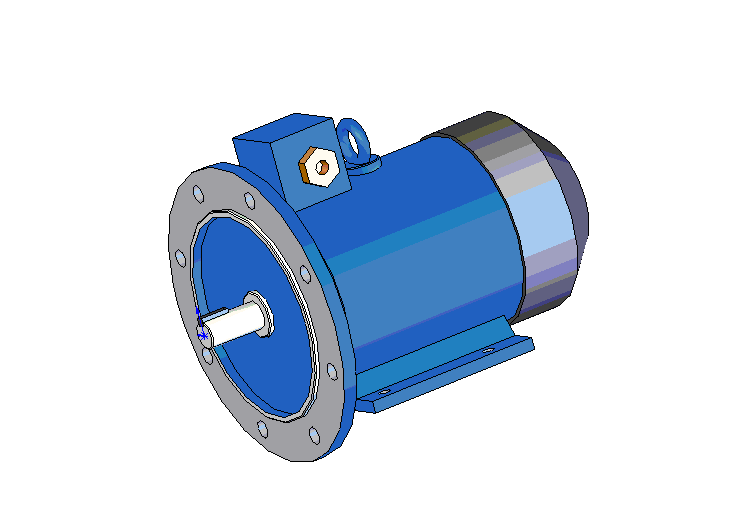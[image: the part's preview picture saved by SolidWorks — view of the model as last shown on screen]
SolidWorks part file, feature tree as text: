
SOLIDWORKS PART (.sldprt)
format: sldprt  version: not decoded by parser v0  size: 766,464 bytes
history: native  units: mm
features: sketch x18, extrude x12, plane x4, cut_extrude x4, chamfer x3, material x1, sweep x1 (+10 scaffold rows collapsed)
feature tree (53):
  scaffold x10  (default folders/planes/origin — collapsed)
  material  "Ст.3 ГОСТ 380-88"
  plane  "Спереди"
  plane  "Сверху"
  plane  "Справа"
  sketch  "Эскиз1"  dims[D1=24.0mm]
  extrude  "Вытянуть1"  Depth=50mm
  sketch  "Эскиз2"  dims[D1=7.0mm D2=7.0mm D3=27.0mm]
  extrude  "Вытянуть2"  Depth=25mm
  sketch  "Эскиз3"  dims[D1=250.0mm]
  extrude  "Вытянуть3"  Depth=12mm
  sketch  "Эскиз4"  dims[D1=180.0mm D2=170.0mm]
  extrude  "Вытянуть4"  Depth=4mm
  sketch  "Эскиз5"  dims[D1=170.0mm D2=40.0mm]
  cut_extrude  "Вырез-Вытянуть1"  Depth=4mm
  chamfer  "Фаска1"  Distance=1mm Angle=45deg
  sketch  "Эскиз6"  dims[c1.D2=15.0mm c1.D1=~150.356167mm c2.D1=22.5deg c2.D3=107.5mm c2.D4=107.5mm c2.D5=107.5mm]
  cut_extrude  "Вырез-Вытянуть2"  [1 undecoded]
  sketch  "Эскиз7"  dims[D1=150.0mm]
  extrude  "Вытянуть5"  Depth=24mm
  sketch  "Эскиз8"  dims[D1=160.0mm]
  extrude  "Вытянуть6"  Depth=167mm
  sketch  "Эскиз9"  dims[D1=166.0mm]
  extrude  "Вытянуть7"  Depth=84mm
  chamfer  "Фаска2"  Distance=34mm Angle=45deg
  sketch  "Эскиз10"  dims[c1.D1=10.0mm c1.D2=84.0mm c1.D3=10.0mm c1.D4=~41.116657mm c2.D4=30.0deg c2.D5=90.0mm c2.D6=58.0mm]
  extrude  "Вытянуть8"  Depth=153mm
  sketch  "Эскиз11"  dims[D2=10.0mm D1=106.0mm D3=70.0mm D4=90.0deg D5=100.0mm D6=206.0mm D7=140.0mm]
  cut_extrude  "Вырез-Вытянуть3"  [1 undecoded]
  sketch  "Эскиз12"  dims[D1=60.0mm D2=60.0mm D3=1.0mm]
  extrude  "Вытянуть9"  Depth=134.5mm
  sketch  "Эскиз13"  dims[D1=35.0mm D2=175.0mm]
  extrude  "Вытянуть10"  Depth=85.5mm
  chamfer  "Фаска3"  Distance=1mm Angle=45deg
  plane  "Плоскость1"  Offset=175mm
  sketch  "Эскиз14"  dims[D1=32.0mm]
  sketch  "Эскиз15"  dims[D1=10.0mm D2=32.0mm]
  sweep  "По траектории1"
  sketch  "Эскиз16"  dims[c1.D1=~12.488278mm c1.D3=18.0mm c2.D1=30.0mm c2.D2=30.0mm]
  extrude  "Вытянуть11"  Depth=8mm
  sketch  "Эскиз17"  dims[D1=~17.851489mm]
  extrude  "Вытянуть12"  Depth=10mm
  sketch  "Эскиз18"  dims[D1=12.0mm]
  cut_extrude  "Вырез-Вытянуть4"  Depth=10mm
decode coverage: 35 of 38 modeling features carry decoded parameters
note: ~ marks probable driven/reference dimensions
note: 2 parameter values undecoded
note: suppression state not decoded; provenance and decode notes live in map.json
